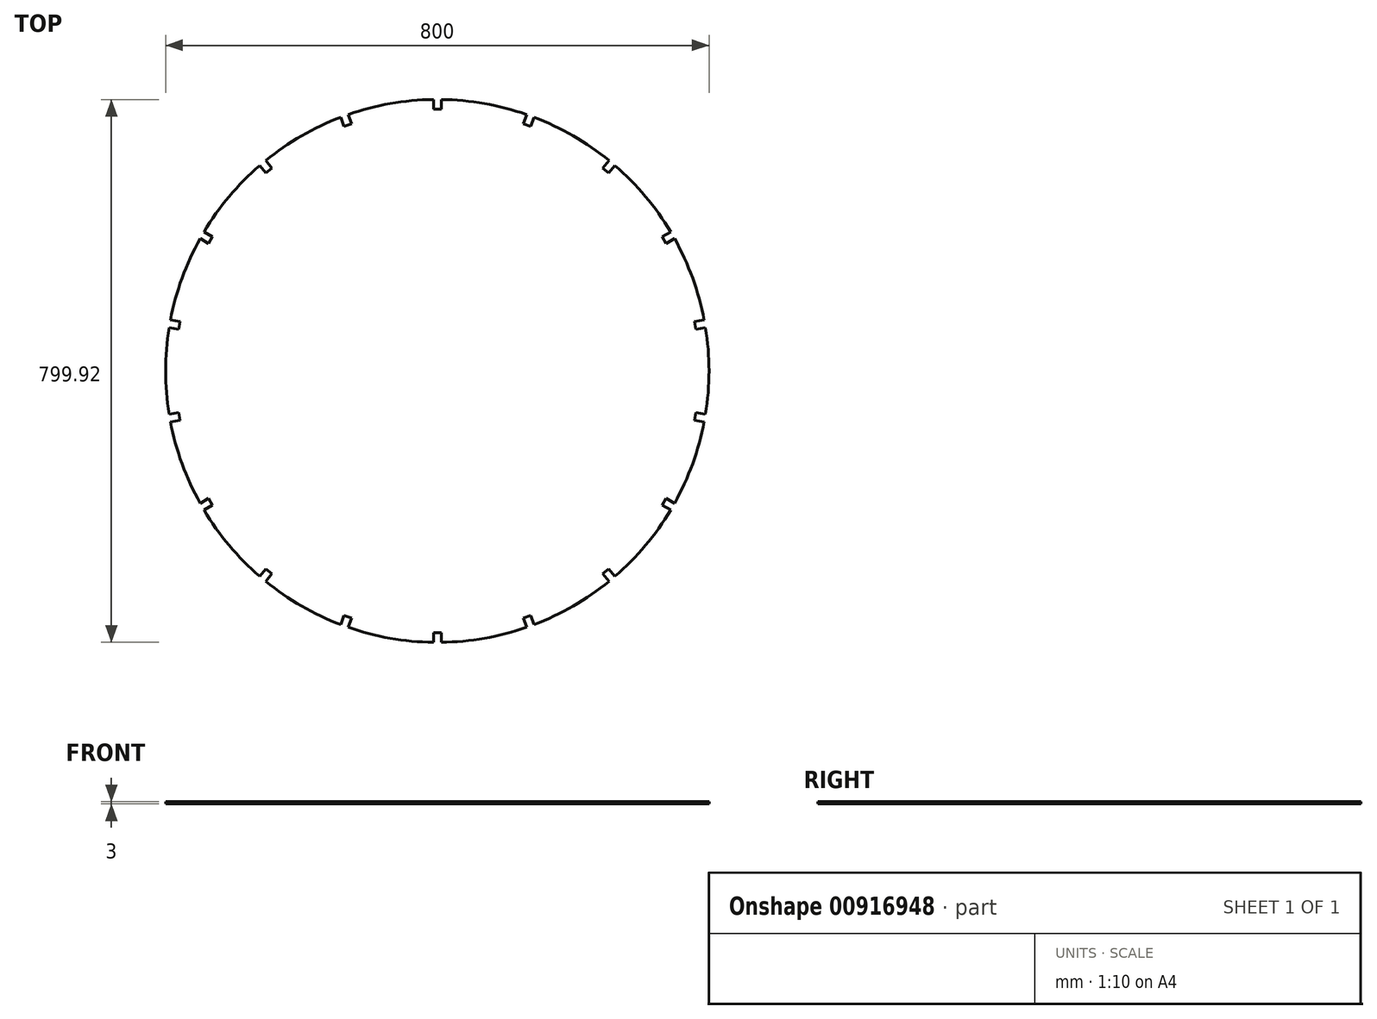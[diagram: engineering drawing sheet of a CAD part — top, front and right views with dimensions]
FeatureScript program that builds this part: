
annotation { "Feature Type Name" : "Feature", "Feature Type Description" : "" }
export const myFeature = defineFeature(function(context is Context, id is Id, definition is map)
    precondition{}
    {
        {
            var Q0;
            Q0=qCreatedBy(makeId("Top.planeOp"),FACE);
            var sketch = newSketch(context, id + "F0", { "sketchPlane" : qUnion([Q0])});
            skArc(sketch, "E0", {"start": v(-5.75, 399.96) * mm, "mid": v(-69.46, 393.92) * mm, "end": v(-131.4, 377.8) * mm});
            skLineSegment(sketch, "E1", {"start": v(0, 400) * mm, "end": v(0, 0) * mm, "construction": true});
            skLineSegment(sketch, "E2.0", {"start": v(-5.75, 400) * mm, "end": v(-5.75, 385.5) * mm});
            skLineSegment(sketch, "E3.0", {"start": v(5.75, 400) * mm, "end": v(5.75, 385.5) * mm});
            skLineSegment(sketch, "E4.0", {"start": v(-5.75, 385.5) * mm, "end": v(5.75, 385.5) * mm});
            skLineSegment(sketch, "E5.1.0", {"start": v(-131.4, 377.84) * mm, "end": v(-126.45, 364.22) * mm});
            skLineSegment(sketch, "E5.1.1", {"start": v(-142.21, 373.91) * mm, "end": v(-137.25, 360.28) * mm});
            skLineSegment(sketch, "E5.1.2", {"start": v(-137.25, 360.28) * mm, "end": v(-126.45, 364.22) * mm});
            skLineSegment(sketch, "E5.2.0", {"start": v(-252.71, 310.11) * mm, "end": v(-243.39, 299) * mm});
            skLineSegment(sketch, "E5.2.1", {"start": v(-261.52, 302.72) * mm, "end": v(-252.2, 291.61) * mm});
            skLineSegment(sketch, "E5.2.2", {"start": v(-252.2, 291.61) * mm, "end": v(-243.39, 299) * mm});
            skLineSegment(sketch, "E5.3.0", {"start": v(-343.54, 204.98) * mm, "end": v(-330.98, 197.73) * mm});
            skLineSegment(sketch, "E5.3.1", {"start": v(-349.29, 195.02) * mm, "end": v(-336.73, 187.77) * mm});
            skLineSegment(sketch, "E5.3.2", {"start": v(-336.73, 187.77) * mm, "end": v(-330.98, 197.73) * mm});
            skLineSegment(sketch, "E5.4.0", {"start": v(-392.92, 75.12) * mm, "end": v(-378.64, 72.6) * mm});
            skLineSegment(sketch, "E5.4.1", {"start": v(-394.92, 63.8) * mm, "end": v(-380.64, 61.28) * mm});
            skLineSegment(sketch, "E5.4.2", {"start": v(-380.64, 61.28) * mm, "end": v(-378.64, 72.6) * mm});
            skLineSegment(sketch, "E5.5.0", {"start": v(-394.92, -63.8) * mm, "end": v(-380.64, -61.28) * mm});
            skLineSegment(sketch, "E5.5.1", {"start": v(-392.92, -75.12) * mm, "end": v(-378.64, -72.6) * mm});
            skLineSegment(sketch, "E5.5.2", {"start": v(-378.64, -72.6) * mm, "end": v(-380.64, -61.28) * mm});
            skLineSegment(sketch, "E5.6.0", {"start": v(-349.29, -195.02) * mm, "end": v(-336.73, -187.77) * mm});
            skLineSegment(sketch, "E5.6.1", {"start": v(-343.54, -204.98) * mm, "end": v(-330.98, -197.73) * mm});
            skLineSegment(sketch, "E5.6.2", {"start": v(-330.98, -197.73) * mm, "end": v(-336.73, -187.77) * mm});
            skLineSegment(sketch, "E5.7.0", {"start": v(-261.52, -302.72) * mm, "end": v(-252.2, -291.61) * mm});
            skLineSegment(sketch, "E5.7.1", {"start": v(-252.71, -310.11) * mm, "end": v(-243.39, -299) * mm});
            skLineSegment(sketch, "E5.7.2", {"start": v(-243.39, -299) * mm, "end": v(-252.2, -291.61) * mm});
            skLineSegment(sketch, "E5.8.0", {"start": v(-142.21, -373.91) * mm, "end": v(-137.25, -360.28) * mm});
            skLineSegment(sketch, "E5.8.1", {"start": v(-131.4, -377.84) * mm, "end": v(-126.45, -364.22) * mm});
            skLineSegment(sketch, "E5.8.2", {"start": v(-126.45, -364.22) * mm, "end": v(-137.25, -360.28) * mm});
            skLineSegment(sketch, "E5.9.0", {"start": v(-5.75, -400) * mm, "end": v(-5.75, -385.5) * mm});
            skLineSegment(sketch, "E5.9.1", {"start": v(5.75, -400) * mm, "end": v(5.75, -385.5) * mm});
            skLineSegment(sketch, "E5.9.2", {"start": v(5.75, -385.5) * mm, "end": v(-5.75, -385.5) * mm});
            skLineSegment(sketch, "E5.10.0", {"start": v(131.4, -377.84) * mm, "end": v(126.45, -364.22) * mm});
            skLineSegment(sketch, "E5.10.1", {"start": v(142.21, -373.91) * mm, "end": v(137.25, -360.28) * mm});
            skLineSegment(sketch, "E5.10.2", {"start": v(137.25, -360.28) * mm, "end": v(126.45, -364.22) * mm});
            skLineSegment(sketch, "E5.11.0", {"start": v(252.71, -310.11) * mm, "end": v(243.39, -299) * mm});
            skLineSegment(sketch, "E5.11.1", {"start": v(261.52, -302.72) * mm, "end": v(252.2, -291.61) * mm});
            skLineSegment(sketch, "E5.11.2", {"start": v(252.2, -291.61) * mm, "end": v(243.39, -299) * mm});
            skLineSegment(sketch, "E5.12.0", {"start": v(343.54, -204.98) * mm, "end": v(330.98, -197.73) * mm});
            skLineSegment(sketch, "E5.12.1", {"start": v(349.29, -195.02) * mm, "end": v(336.73, -187.77) * mm});
            skLineSegment(sketch, "E5.12.2", {"start": v(336.73, -187.77) * mm, "end": v(330.98, -197.73) * mm});
            skLineSegment(sketch, "E5.13.0", {"start": v(392.92, -75.12) * mm, "end": v(378.64, -72.6) * mm});
            skLineSegment(sketch, "E5.13.1", {"start": v(394.92, -63.8) * mm, "end": v(380.64, -61.28) * mm});
            skLineSegment(sketch, "E5.13.2", {"start": v(380.64, -61.28) * mm, "end": v(378.64, -72.6) * mm});
            skLineSegment(sketch, "E5.14.0", {"start": v(394.92, 63.8) * mm, "end": v(380.64, 61.28) * mm});
            skLineSegment(sketch, "E5.14.1", {"start": v(392.92, 75.12) * mm, "end": v(378.64, 72.6) * mm});
            skLineSegment(sketch, "E5.14.2", {"start": v(378.64, 72.6) * mm, "end": v(380.64, 61.28) * mm});
            skLineSegment(sketch, "E5.15.0", {"start": v(349.29, 195.02) * mm, "end": v(336.73, 187.77) * mm});
            skLineSegment(sketch, "E5.15.1", {"start": v(343.54, 204.98) * mm, "end": v(330.98, 197.73) * mm});
            skLineSegment(sketch, "E5.15.2", {"start": v(330.98, 197.73) * mm, "end": v(336.73, 187.77) * mm});
            skLineSegment(sketch, "E5.16.0", {"start": v(261.52, 302.72) * mm, "end": v(252.2, 291.61) * mm});
            skLineSegment(sketch, "E5.16.1", {"start": v(252.71, 310.11) * mm, "end": v(243.39, 299) * mm});
            skLineSegment(sketch, "E5.16.2", {"start": v(243.39, 299) * mm, "end": v(252.2, 291.61) * mm});
            skLineSegment(sketch, "E5.17.0", {"start": v(142.21, 373.91) * mm, "end": v(137.25, 360.28) * mm});
            skLineSegment(sketch, "E5.17.1", {"start": v(131.4, 377.84) * mm, "end": v(126.45, 364.22) * mm});
            skLineSegment(sketch, "E5.17.2", {"start": v(126.45, 364.22) * mm, "end": v(137.25, 360.28) * mm});
            skArc(sketch, "E6.trimOffspring", {"start": v(-142.2, 373.87) * mm, "mid": v(-200, 346.41) * mm, "end": v(-252.68, 310.08) * mm});
            skArc(sketch, "E7.trimOffspring", {"start": v(-261.5, 302.7) * mm, "mid": v(-306.42, 257.12) * mm, "end": v(-343.5, 204.96) * mm});
            skArc(sketch, "E8.trimOffspring", {"start": v(-349.25, 195) * mm, "mid": v(-375.88, 136.8) * mm, "end": v(-392.88, 75.11) * mm});
            skArc(sketch, "E9.trimOffspring", {"start": v(131.4, 377.8) * mm, "mid": v(69.46, 393.92) * mm, "end": v(5.75, 399.96) * mm});
            skArc(sketch, "E10.trimOffspring", {"start": v(-394.88, 63.79) * mm, "mid": v(-400, 0) * mm, "end": v(-394.88, -63.79) * mm});
            skArc(sketch, "E11.trimOffspring", {"start": v(-392.88, -75.11) * mm, "mid": v(-375.88, -136.8) * mm, "end": v(-349.25, -195) * mm});
            skArc(sketch, "E12.trimOffspring", {"start": v(-343.5, -204.96) * mm, "mid": v(-306.42, -257.12) * mm, "end": v(-261.5, -302.7) * mm});
            skArc(sketch, "E13.trimOffspring", {"start": v(-252.68, -310.08) * mm, "mid": v(-200, -346.41) * mm, "end": v(-142.2, -373.87) * mm});
            skArc(sketch, "E14.trimOffspring", {"start": v(-131.4, -377.8) * mm, "mid": v(-69.46, -393.92) * mm, "end": v(-5.75, -399.96) * mm});
            skArc(sketch, "E15.trimOffspring", {"start": v(5.75, -399.96) * mm, "mid": v(69.46, -393.92) * mm, "end": v(131.4, -377.8) * mm});
            skArc(sketch, "E16.trimOffspring", {"start": v(142.2, -373.87) * mm, "mid": v(200, -346.41) * mm, "end": v(252.68, -310.08) * mm});
            skArc(sketch, "E17.trimOffspring", {"start": v(261.5, -302.7) * mm, "mid": v(306.42, -257.12) * mm, "end": v(343.5, -204.96) * mm});
            skArc(sketch, "E18.trimOffspring", {"start": v(349.25, -195) * mm, "mid": v(375.88, -136.8) * mm, "end": v(392.88, -75.11) * mm});
            skArc(sketch, "E19.trimOffspring", {"start": v(394.88, -63.79) * mm, "mid": v(400, 0) * mm, "end": v(394.88, 63.79) * mm});
            skArc(sketch, "E20.trimOffspring", {"start": v(392.88, 75.11) * mm, "mid": v(375.88, 136.8) * mm, "end": v(349.25, 195) * mm});
            skArc(sketch, "E21.trimOffspring", {"start": v(343.5, 204.96) * mm, "mid": v(306.42, 257.12) * mm, "end": v(261.5, 302.7) * mm});
            skArc(sketch, "E22.trimOffspring", {"start": v(252.68, 310.08) * mm, "mid": v(200, 346.41) * mm, "end": v(142.2, 373.87) * mm});
            skSolve(sketch);
        }
        {
            var Q0;
            {var subQ41=sQuery(id+"F0.wireOp",EDGE,"E0");Q0=makeQuery(id+"F0.imprint","IMPRINT",FACE,{"disambiguationData":[TD([[makeQuery(id+"F0.imprint","IMPRINT",EDGE,{"derivedFrom":subQ41}),1.0]])]});}
            extrude(context, id + "F1", {"entities" : qUnion([Q0]), "depth" : 3 * mm, "offsetDistance" : 25 * mm});
        }
    });
